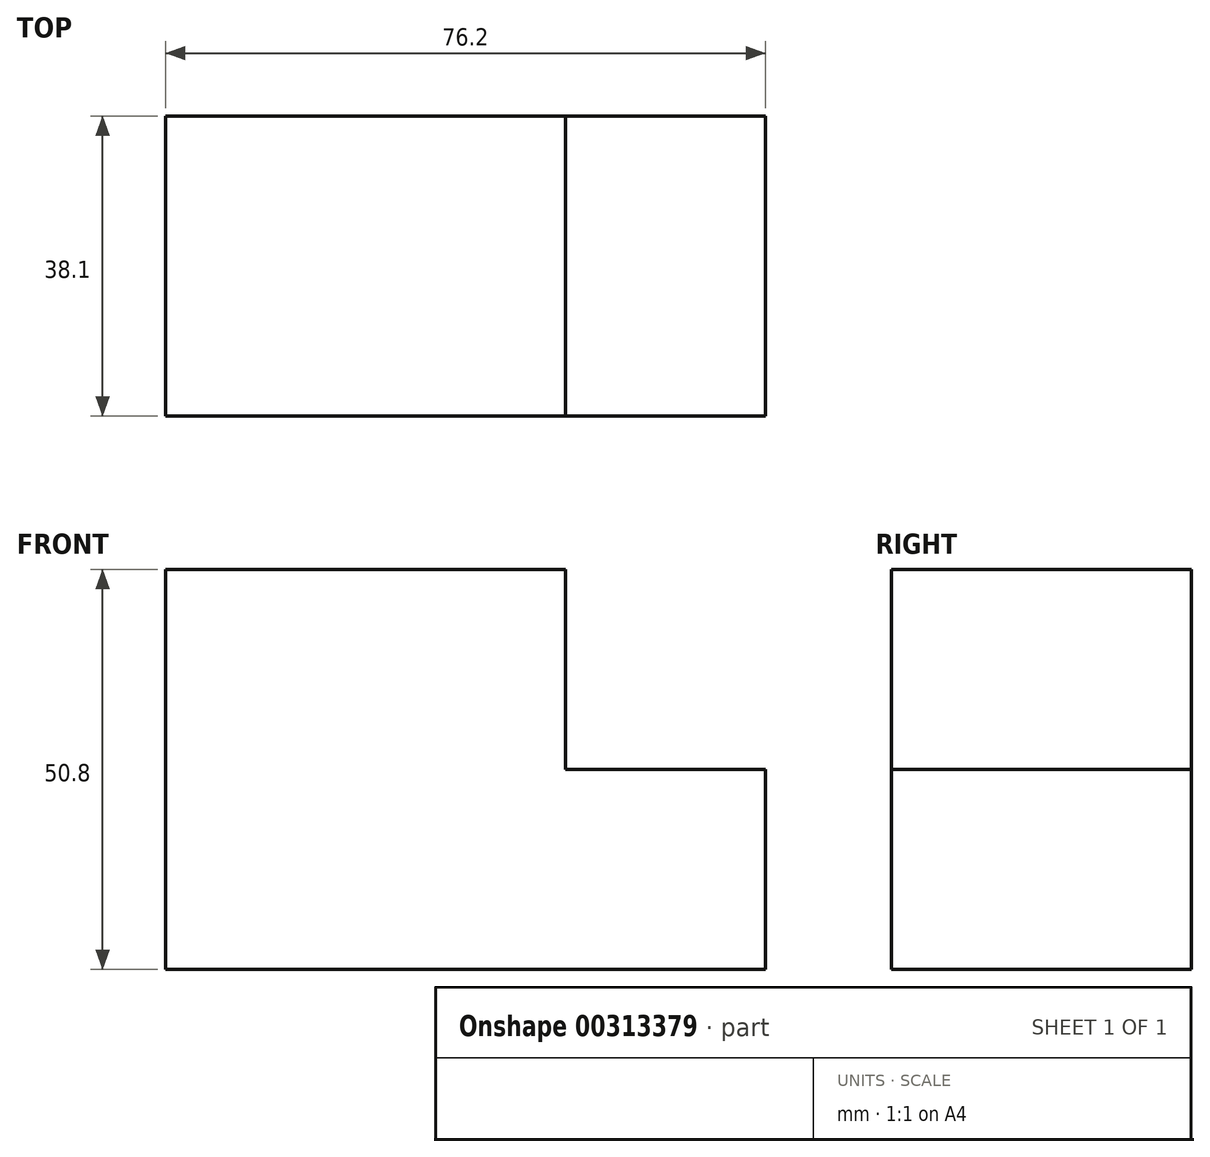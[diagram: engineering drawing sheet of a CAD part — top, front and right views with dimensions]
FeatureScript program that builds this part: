
annotation { "Feature Type Name" : "Feature", "Feature Type Description" : "" }
export const myFeature = defineFeature(function(context is Context, id is Id, definition is map)
    precondition{}
    {
        {
            var Q0;
            Q0=qCreatedBy(makeId("Front.planeOp"),FACE);
            var sketch = newSketch(context, id + "F0", { "sketchPlane" : qUnion([Q0])});
            skLineSegment(sketch, "E0", {"start": v(-34.68, -24.96) * mm, "end": v(41.52, -24.96) * mm});
            skLineSegment(sketch, "E1", {"start": v(41.52, -24.96) * mm, "end": v(41.52, 0.44) * mm});
            skLineSegment(sketch, "E2", {"start": v(41.52, 0.44) * mm, "end": v(16.12, 0.44) * mm});
            skLineSegment(sketch, "E3", {"start": v(16.12, 0.44) * mm, "end": v(16.12, 25.84) * mm});
            skLineSegment(sketch, "E4", {"start": v(16.12, 25.84) * mm, "end": v(-34.68, 25.84) * mm});
            skLineSegment(sketch, "E5", {"start": v(-34.68, 25.84) * mm, "end": v(-34.68, -24.96) * mm});
            skSolve(sketch);
        }
        {
            var Q0;
            Q0 = qSketchRegion(id + "F0", true);
            extrude(context, id + "F1", {"entities" : qUnion([Q0]), "oppositeDirection" : true, "depth" : 38.1 * mm});
        }
    });
